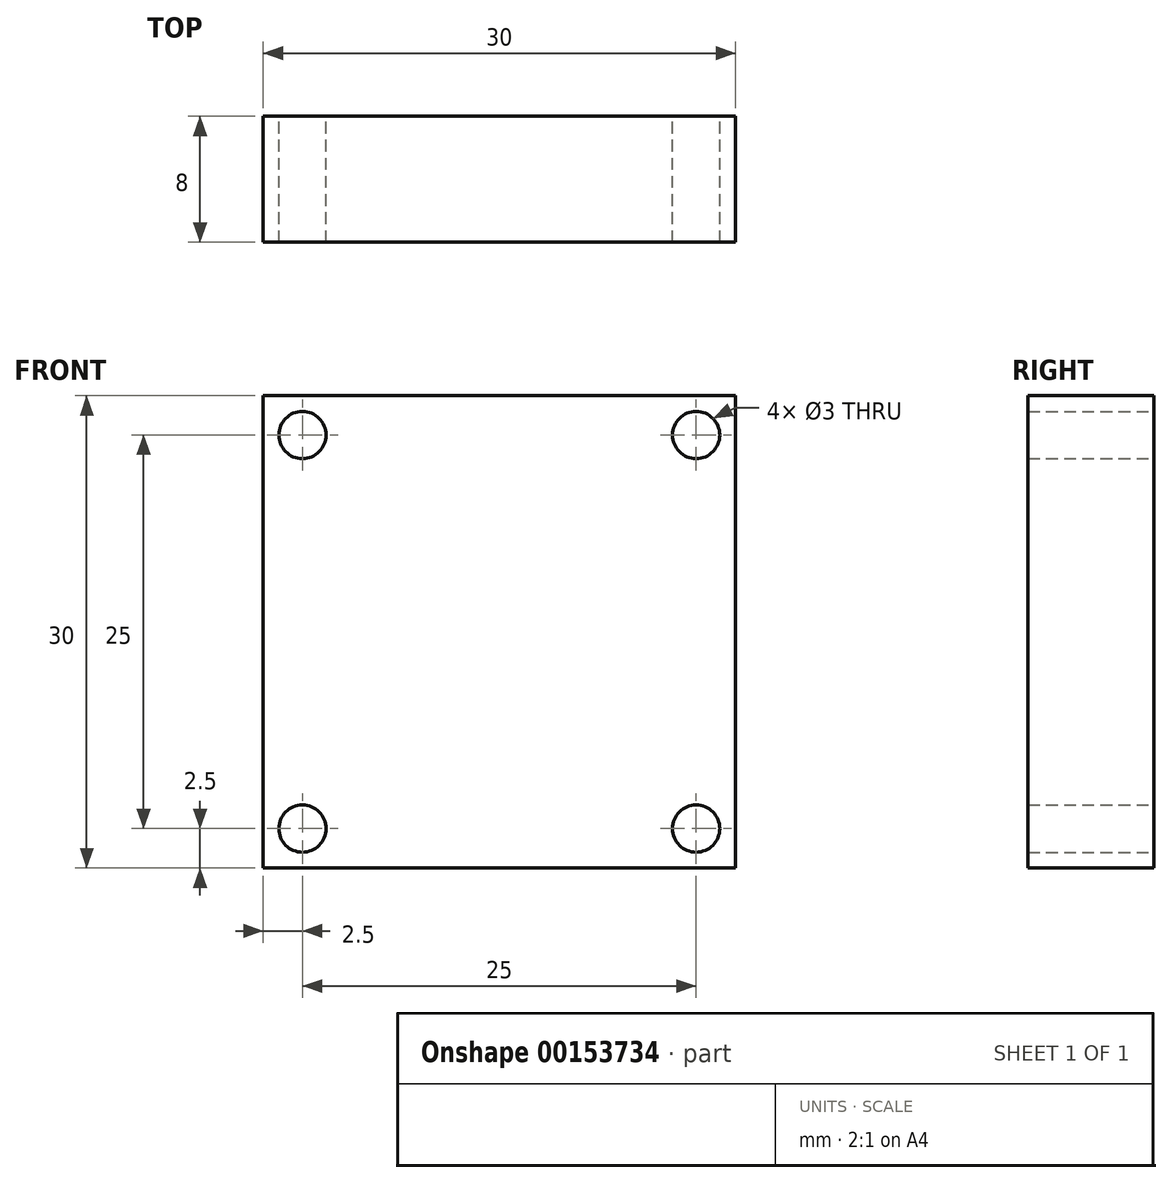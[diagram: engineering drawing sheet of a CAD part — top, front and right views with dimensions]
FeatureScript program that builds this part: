
annotation { "Feature Type Name" : "Feature", "Feature Type Description" : "" }
export const myFeature = defineFeature(function(context is Context, id is Id, definition is map)
    precondition{}
    {
        {
            var Q0;
            Q0=qCreatedBy(makeId("Front.planeOp"),FACE);
            var sketch = newSketch(context, id + "F0", { "sketchPlane" : qUnion([Q0])});
            skLineSegment(sketch, "E0.bottom", {"start": v(0, 0) * mm, "end": v(30, 0) * mm});
            skLineSegment(sketch, "E0.top", {"start": v(0, 30) * mm, "end": v(30, 30) * mm});
            skLineSegment(sketch, "E0.left", {"start": v(0, 0) * mm, "end": v(0, 30) * mm});
            skLineSegment(sketch, "E0.right", {"start": v(30, 0) * mm, "end": v(30, 30) * mm});
            skLineSegment(sketch, "E1.0", {"start": v(5, 25) * mm, "end": v(25, 25) * mm, "construction": true});
            skLineSegment(sketch, "E1.1", {"start": v(5, 5) * mm, "end": v(5, 25) * mm, "construction": true});
            skLineSegment(sketch, "E1.2", {"start": v(5, 5) * mm, "end": v(25, 5) * mm, "construction": true});
            skLineSegment(sketch, "E1.3", {"start": v(25, 5) * mm, "end": v(25, 25) * mm, "construction": true});
            skLineSegment(sketch, "E2.bottom", {"start": v(5, 25) * mm, "end": v(0, 25) * mm, "construction": true});
            skLineSegment(sketch, "E2.top", {"start": v(5, 30) * mm, "end": v(0, 30) * mm, "construction": true});
            skLineSegment(sketch, "E2.left", {"start": v(5, 25) * mm, "end": v(5, 30) * mm, "construction": true});
            skLineSegment(sketch, "E2.right", {"start": v(0, 25) * mm, "end": v(0, 30) * mm, "construction": true});
            skPoint(sketch, "E3", {"position": v(2.5, 30) * mm});
            skPoint(sketch, "E4", {"position": v(0, 27.5) * mm});
            skCircle(sketch, "E5", {"center": v(2.5, 27.5) * mm, "radius": 1.5 * mm});
            skPoint(sketch, "E6", {"position": v(0, 15) * mm});
            skPoint(sketch, "E7", {"position": v(15, 0) * mm});
            skLineSegment(sketch, "E8", {"start": v(15, 0) * mm, "end": v(15, 42.26) * mm, "construction": true});
            skLineSegment(sketch, "E9", {"start": v(0, 15) * mm, "end": v(46.46, 15) * mm, "construction": true});
            skCircle(sketch, "E10.MirrorC", {"center": v(27.5, 27.5) * mm, "radius": 1.5 * mm});
            skCircle(sketch, "E11.MirrorC", {"center": v(2.5, 2.5) * mm, "radius": 1.5 * mm});
            skCircle(sketch, "E12.MirrorC", {"center": v(27.5, 2.5) * mm, "radius": 1.5 * mm});
            skSolve(sketch);
        }
        {
            var Q0;
            Q0 = qSketchRegion(id + "F0", true);
            extrude(context, id + "F1", {"entities" : qUnion([Q0]), "depth" : 8 * mm});
        }
    });
